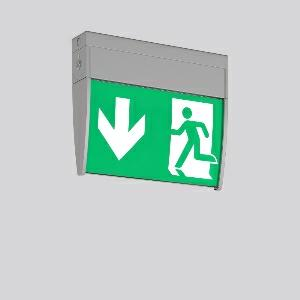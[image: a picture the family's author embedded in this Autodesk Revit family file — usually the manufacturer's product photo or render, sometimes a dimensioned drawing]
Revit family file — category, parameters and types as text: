
# Revit family: gsun_d_672219_004_1_07_ae0f
name_source: partatom
category: Lighting Fixtures
units: mm (PartAtom-declared; Revit-internal decimal feet)

## family parameters
Cut with Voids When Loaded = No
Host = Face
Light Source = No
Part Type = Normal
Room Calculation Point = No
Round Connector Dimension = Use Diameter
Shared = No

## types (1)
- GSUN D
    Apparent Load = 0 VA
    Default Elevation = 1800 mm
    Description = Series: GSUN D
Luminaire for escape route identification. Housing: extruded aluminium profile, powder-coated. 4 legends and 1 white lay in plastic sheet included. Universal mounting kit for ceiling and wall surface mounting. Electronic ballast included. Self-contained system with automatic self-test and feedback via DALI bus, only to RZB DALI monitoring system. 
Colour: silver, matt (approx. RAL 9006)
Length: 247 mm
Width: 45 mm
Height: 200 mm
Weight: 0.9 kg
Operating mode: maintained power mode
Viewing Distance: 24 m
Duration time: 3 h
Lamp: LED
Socket: without socket
Colour temperature: 4000K
System power: 4.7 W
Control gear: Regulated power supply
Protection class: I
Type of protection: IP 30
    Height = 200 mm  [stored 0.656168 ft]
    Lamp = 0 x
    Length = 247 mm
    Luminous efficacy = 0 lm/W
    Manufacturer = RZB
    ModVariant = No
    Model = 672219.004.1.07
    Mounting Place = Ceiling, Wall
    Mounting Type = Surface mounted
    Number of Poles = 1
    OnlyDefault = Yes
    Power Factor = 1
    Product Name = GSUN D
    Product group = Surface mounted ceiling and wall luminaires
    ProductGroupID = 305
    Protection Class = Protection class I
    Protection Degree = IP 30
    RLX_Detail_Level = 1
    RLX_Emergency_Light_Flux = 0 lm
    RLX_Emergency_Type = 0
    RLX_Emergency_Type_DB = No
    RlxData = <blob elided: 32549 chars, md5=b07b143f>
    Standby Power = 0 W
    System Light Flux = 0 lm
    System Power = 0 W
    Type Comments = Product without accessories
    Type Image = 652219.004.jpg
    URL = http://relux.com
    VarID = ---
    Voltage = 230 V
    Voltage Range = 220-240 V
    Weight = 0.00 kg
    Width = 45 mm

note: [stored X ft] marks values corroborated as IEEE doubles in the binary element streams (Revit-internal decimal feet)

## geometry (parser evidence)
native form markers: Blend x4, Sweep x11
no freeform markers — native parametric forms only
